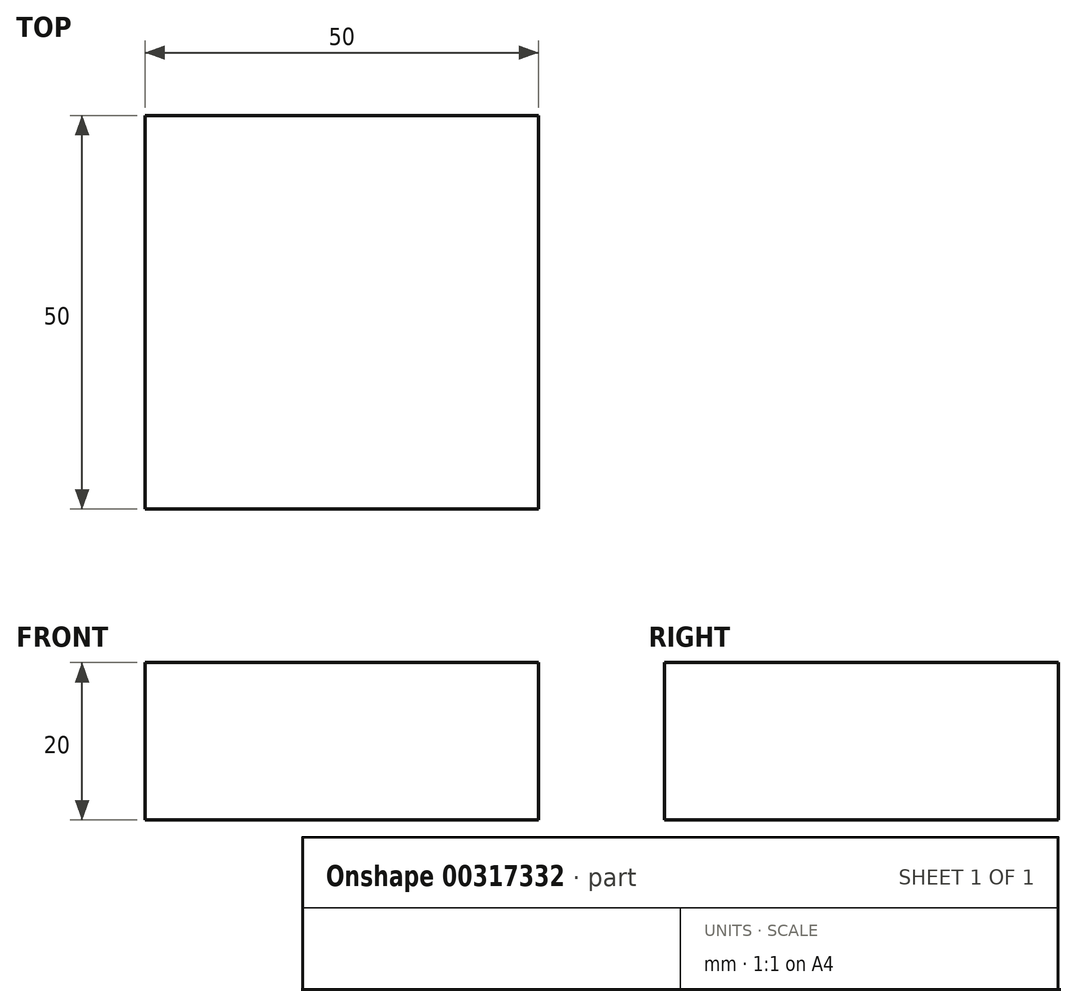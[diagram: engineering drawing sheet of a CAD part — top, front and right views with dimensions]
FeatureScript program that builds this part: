
annotation { "Feature Type Name" : "Feature", "Feature Type Description" : "" }
export const myFeature = defineFeature(function(context is Context, id is Id, definition is map)
    precondition{}
    {
        {
            var Q0;
            Q0=qCreatedBy(makeId("Front.planeOp"),FACE);
            var sketch = newSketch(context, id + "F0", { "sketchPlane" : qUnion([Q0])});
            skLineSegment(sketch, "E0.bottom", {"start": v(-25, 10) * mm, "end": v(25, 10) * mm});
            skLineSegment(sketch, "E0.top", {"start": v(-25, -10) * mm, "end": v(25, -10) * mm});
            skLineSegment(sketch, "E0.left", {"start": v(-25, 10) * mm, "end": v(-25, -10) * mm});
            skLineSegment(sketch, "E0.right", {"start": v(25, 10) * mm, "end": v(25, -10) * mm});
            skPoint(sketch, "E0.middle", {"position": v(0, 0) * mm});
            skSolve(sketch);
        }
        {
            var Q0;
            Q0=makeQuery(id+"F0.imprint","IMPRINT",FACE,{"disambiguationData":[TD([[makeQuery(id+"F0.imprint","IMPRINT",EDGE,{"derivedFrom":sQuery(id+"F0.wireOp",EDGE,"E0.bottom")}),-1.0]])]});
            extrude(context, id + "F1", {"entities" : qUnion([Q0]), "depth" : 50 * mm});
        }
    });
